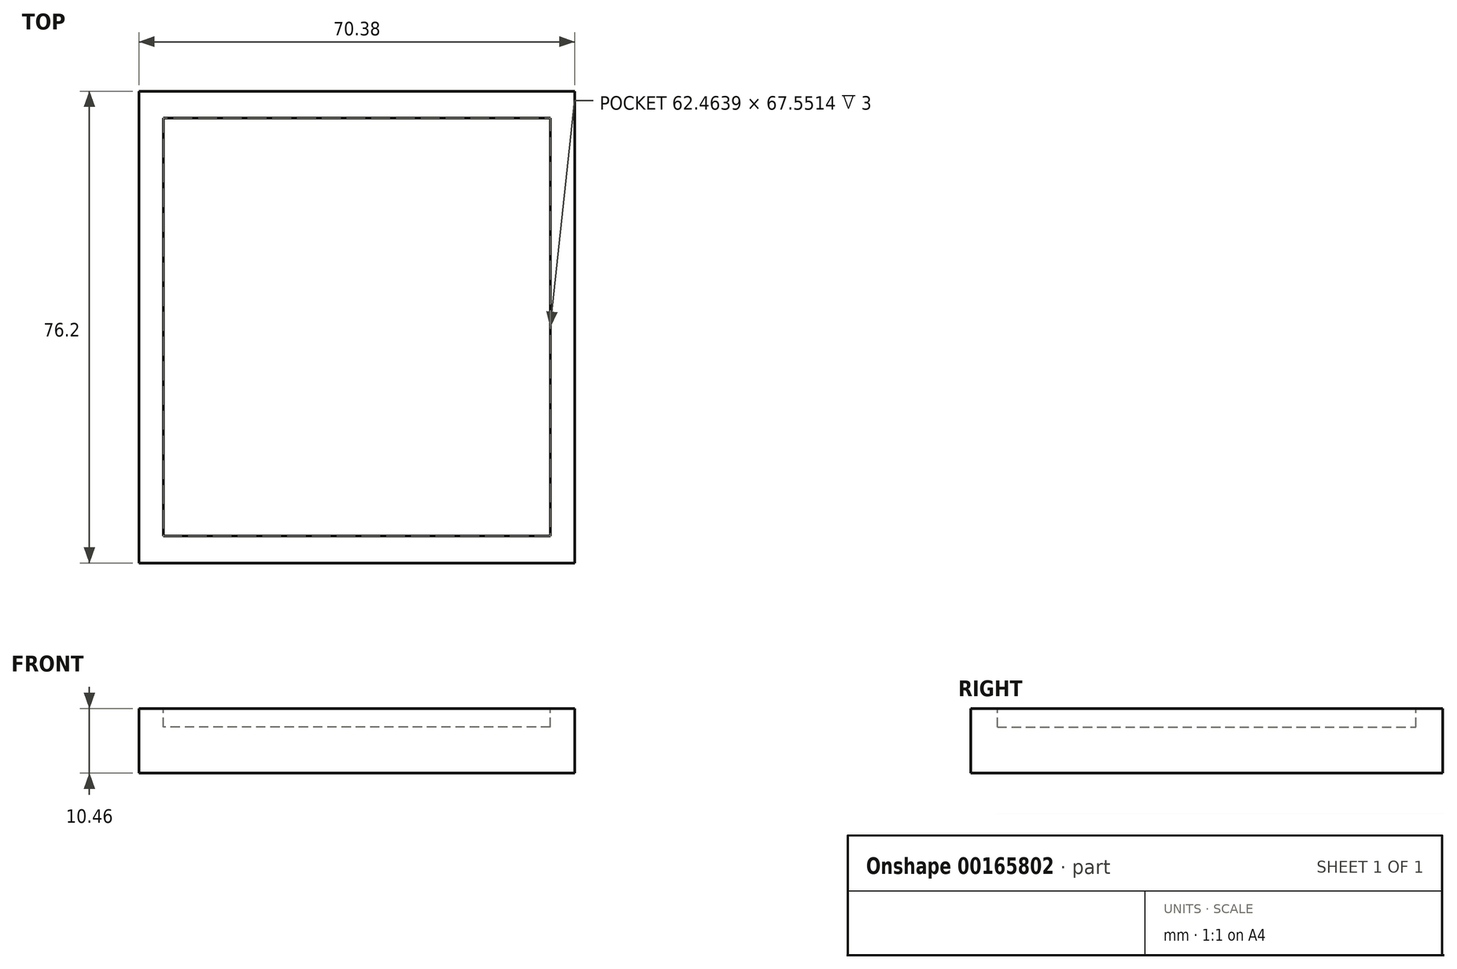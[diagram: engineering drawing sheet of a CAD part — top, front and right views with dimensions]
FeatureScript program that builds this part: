
annotation { "Feature Type Name" : "Feature", "Feature Type Description" : "" }
export const myFeature = defineFeature(function(context is Context, id is Id, definition is map)
    precondition{}
    {
        {
            var Q0;
            Q0=qCreatedBy(makeId("Front.planeOp"),FACE);
            var sketch = newSketch(context, id + "F0", { "sketchPlane" : qUnion([Q0])});
            skLineSegment(sketch, "E0.bottom", {"start": v(-25.3, 4.38) * mm, "end": v(45.08, 4.38) * mm});
            skLineSegment(sketch, "E0.top", {"start": v(-25.3, -6.08) * mm, "end": v(45.08, -6.08) * mm});
            skLineSegment(sketch, "E0.left", {"start": v(-25.3, 4.38) * mm, "end": v(-25.3, -6.08) * mm});
            skLineSegment(sketch, "E0.right", {"start": v(45.08, 4.38) * mm, "end": v(45.08, -6.08) * mm});
            skSolve(sketch);
        }
        {
            var Q0;
            Q0 = qSketchRegion(id + "F0", true);
            extrude(context, id + "F1", {"entities" : qUnion([Q0]), "depth" : 76.2 * mm});
        }
        {
            var Q0;
            Q0=makeQuery(id+"F1.opExtrude","SWEPT_FACE",FACE,{"disambiguationData":[OSD([sQuery(id+"F0.wireOp",EDGE,"E0.bottom")])]});
            var sketch = newSketch(context, id + "F2", { "sketchPlane" : qUnion([Q0])});
            skLineSegment(sketch, "E1.bottom", {"start": v(41.12, -71.88) * mm, "end": v(-21.34, -71.88) * mm});
            skLineSegment(sketch, "E1.top", {"start": v(41.12, -4.32) * mm, "end": v(-21.34, -4.32) * mm});
            skLineSegment(sketch, "E1.left", {"start": v(41.12, -71.88) * mm, "end": v(41.12, -4.32) * mm});
            skLineSegment(sketch, "E1.right", {"start": v(-21.34, -71.88) * mm, "end": v(-21.34, -4.32) * mm});
            skPoint(sketch, "E1.middle", {"position": v(9.9, -38.1) * mm});
            skPoint(sketch, "E1.middle.positionSnap0", {"position": v(9.9, -76.2) * mm});
            skPoint(sketch, "E1.middle.positionSnap1", {"position": v(-25.3, -38.1) * mm});
            skPoint(sketch, "E1.centerSnap0", {"position": v(9.9, -76.2) * mm});
            skPoint(sketch, "E1.centerSnap1", {"position": v(-25.3, -38.1) * mm});
            skSolve(sketch);
        }
        {
            var Q0;
            Q0 = qSketchRegion(id + "F2", true);
            extrude(context, id + "F3", {"entities" : qUnion([Q0]), "operationType" : NewBodyOperationType.REMOVE, "oppositeDirection" : true, "depth" : 3 * mm});
        }
    });
